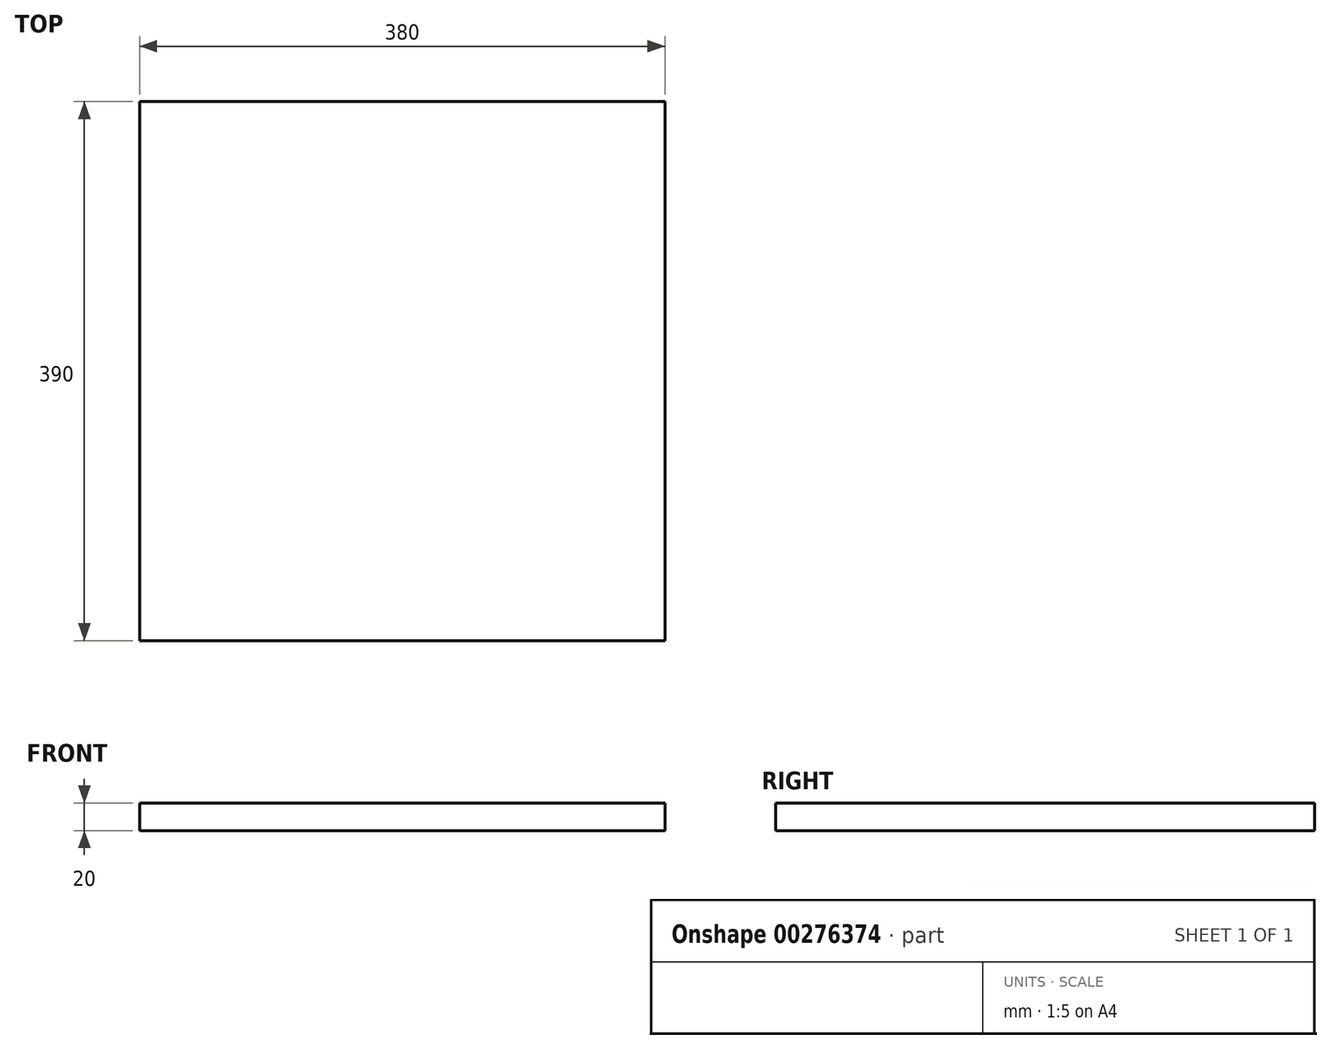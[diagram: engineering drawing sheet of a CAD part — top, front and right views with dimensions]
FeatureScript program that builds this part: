
annotation { "Feature Type Name" : "Feature", "Feature Type Description" : "" }
export const myFeature = defineFeature(function(context is Context, id is Id, definition is map)
    precondition{}
    {
        {
            var Q0;
            Q0=qCreatedBy(makeId("Top.planeOp"),FACE);
            var sketch = newSketch(context, id + "F0", { "sketchPlane" : qUnion([Q0])});
            skLineSegment(sketch, "E0.bottom", {"start": v(-183.8, 224.94) * mm, "end": v(196.2, 224.94) * mm});
            skLineSegment(sketch, "E0.top", {"start": v(-183.8, -165.06) * mm, "end": v(196.2, -165.06) * mm});
            skLineSegment(sketch, "E0.left", {"start": v(-183.8, 224.94) * mm, "end": v(-183.8, -165.06) * mm});
            skLineSegment(sketch, "E0.right", {"start": v(196.2, 224.94) * mm, "end": v(196.2, -165.06) * mm});
            skSolve(sketch);
        }
        {
            var Q0;
            Q0 = qSketchRegion(id + "F0", true);
            extrude(context, id + "F1", {"entities" : qUnion([Q0]), "depth" : 20 * mm});
        }
    });
